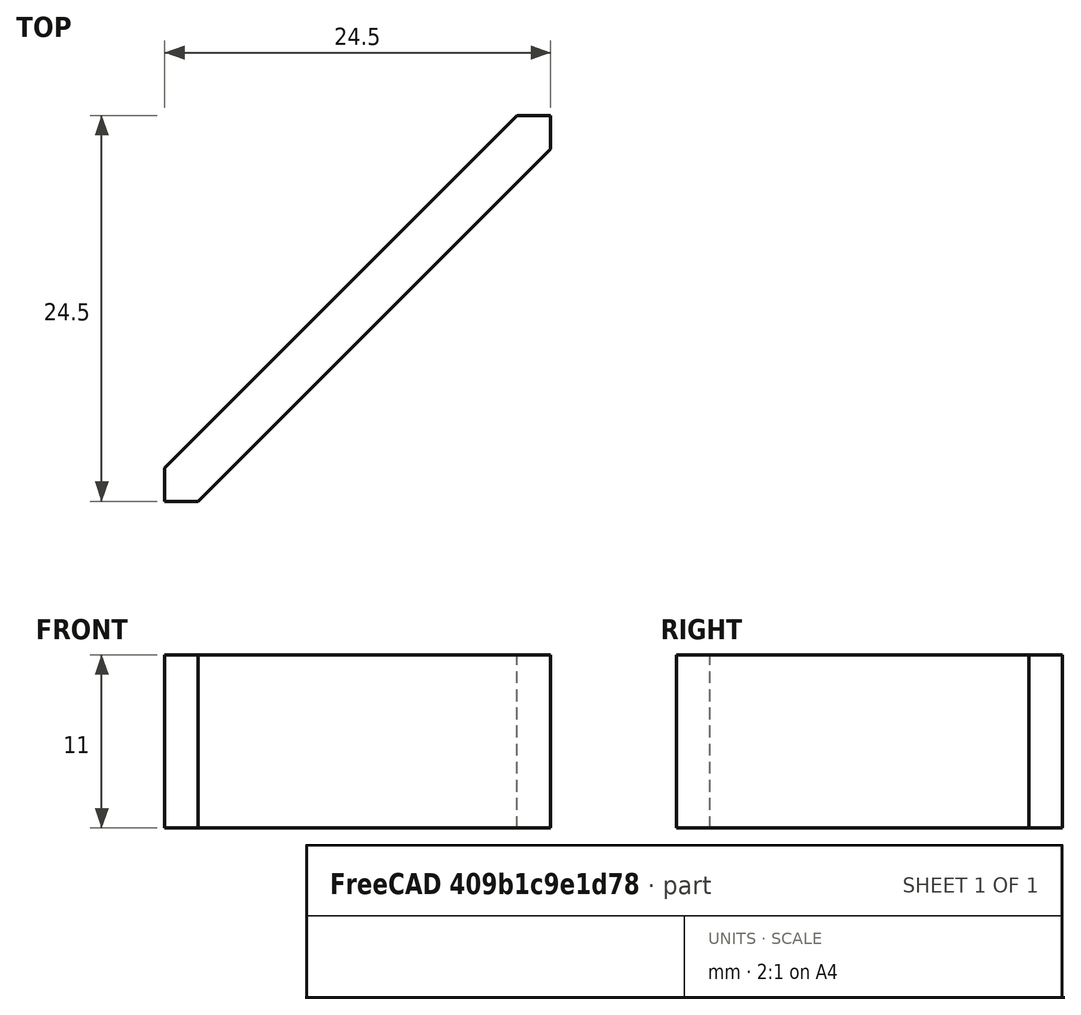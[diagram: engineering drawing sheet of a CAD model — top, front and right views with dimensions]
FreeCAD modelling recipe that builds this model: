
FCSTD DOCUMENT  (FreeCAD 0.21R33694 (Git))
Label: kumiko_inlay_diagonal
License: All rights reserved
LicenseURL: https://en.wikipedia.org/wiki/All_rights_reserved
objects: Sketcher::SketchObject×1, PartDesign::Pad×1, PartDesign::Body×1, App::Link×1
note: 4 computed .brp shape members not serialized (recipe doc carries the construction recipe); baked Part::Feature solids carry a one-line shape summary decoded from their .brp
EXTERNAL_REF file=../../master_kumiko_box.FCStd obj=Spreadsheet

FEATURE [Sketcher::SketchObject] Sketch098  label="long_diagonal_profile"
  FullyConstrained = true
  MapMode = 5
  Support = -> [XY_Plane084]
  expr: Constraints[10] = <<SpreadSheet>>.kumiko_thickness * sqrt(2) / 2
  expr: Constraints[13] = <<SpreadSheet>>.kumiko_thickness * sqrt(2) / 2
  expr: Constraints[1] = 0
  expr: Constraints[2] = 0
  expr: Constraints[3] = <<SpreadSheet>>.kumiko_thickness * sqrt(2) / 2
  expr: Constraints[6] = <<SpreadSheet>>.kumiko_thickness * sqrt(2) / 2
  expr: Constraints[8] = <<SpreadSheet>>.kumiko_grid_size - <<SpreadSheet>>.kumiko_thickness
  expr: Constraints[9] = <<SpreadSheet>>.kumiko_grid_size - <<SpreadSheet>>.kumiko_thickness
  sketch-geometry (6):
    g0: LineSegment StartX=3.6e-15 StartY=0 StartZ=0 EndX=3.6e-15 EndY=2.12132 EndZ=0
    g1: LineSegment StartX=3.6e-15 StartY=0 StartZ=0 EndX=2.12132 EndY=0 EndZ=0
    g2: LineSegment StartX=24.5 StartY=24.5 StartZ=0 EndX=24.5 EndY=22.3787 EndZ=0
    g3: LineSegment StartX=24.5 StartY=24.5 StartZ=0 EndX=22.3787 EndY=24.5 EndZ=0
    g4: LineSegment StartX=2.12132 StartY=0 StartZ=0 EndX=24.5 EndY=22.3787 EndZ=0
    g5: LineSegment StartX=22.3787 StartY=24.5 StartZ=0 EndX=3.6e-15 EndY=2.12132 EndZ=0
  constraints (18):
    c: Vertical(g0)
    c: DistanceY(g-1,g0) = 0
    c: DistanceX(g-1,g0) = 0
    c: DistanceY(g0,g0) = 2.12132
    c: Coincident(g1,g0)
    c: Horizontal(g1)
    c: DistanceX(g1,g1) = 2.12132
    c: Vertical(g2)
    c: DistanceX(g-1,g2) = 24.5
    c: DistanceY(g-1,g2) = 24.5
    c: DistanceY(g2,g2) = 2.12132
    c: Coincident(g3,g2)
    c: Horizontal(g3)
    c: DistanceX(g3,g3) = 2.12132
    c: Coincident(g4,g1)
    c: Coincident(g4,g2)
    c: Coincident(g5,g3)
    c: Coincident(g5,g0)
FEATURE [PartDesign::Pad] Pad047  label="long_diagonal_extrusion"
  Direction = (0,0,1)
  Length = 11
  Length2 = 10
  Profile = -> Sketch098
  ReferenceAxis = -> Sketch098 [N_Axis]
  Type = 0
  expr: Length = <<SpreadSheet>>.kumiko_hight
FEATURE [PartDesign::Body] Body063  label="long_diagonal_body"
  Group = -> [Sketch098,Pad047]
  Origin = -> Origin084
  Tip = -> Pad047
  expr: .Placement.Base.z = 0
FEATURE [App::Link] Link  label="SpreadSheet"
  LinkedObject = -> <external ../../master_kumiko_box.FCStd>#Spreadsheet
